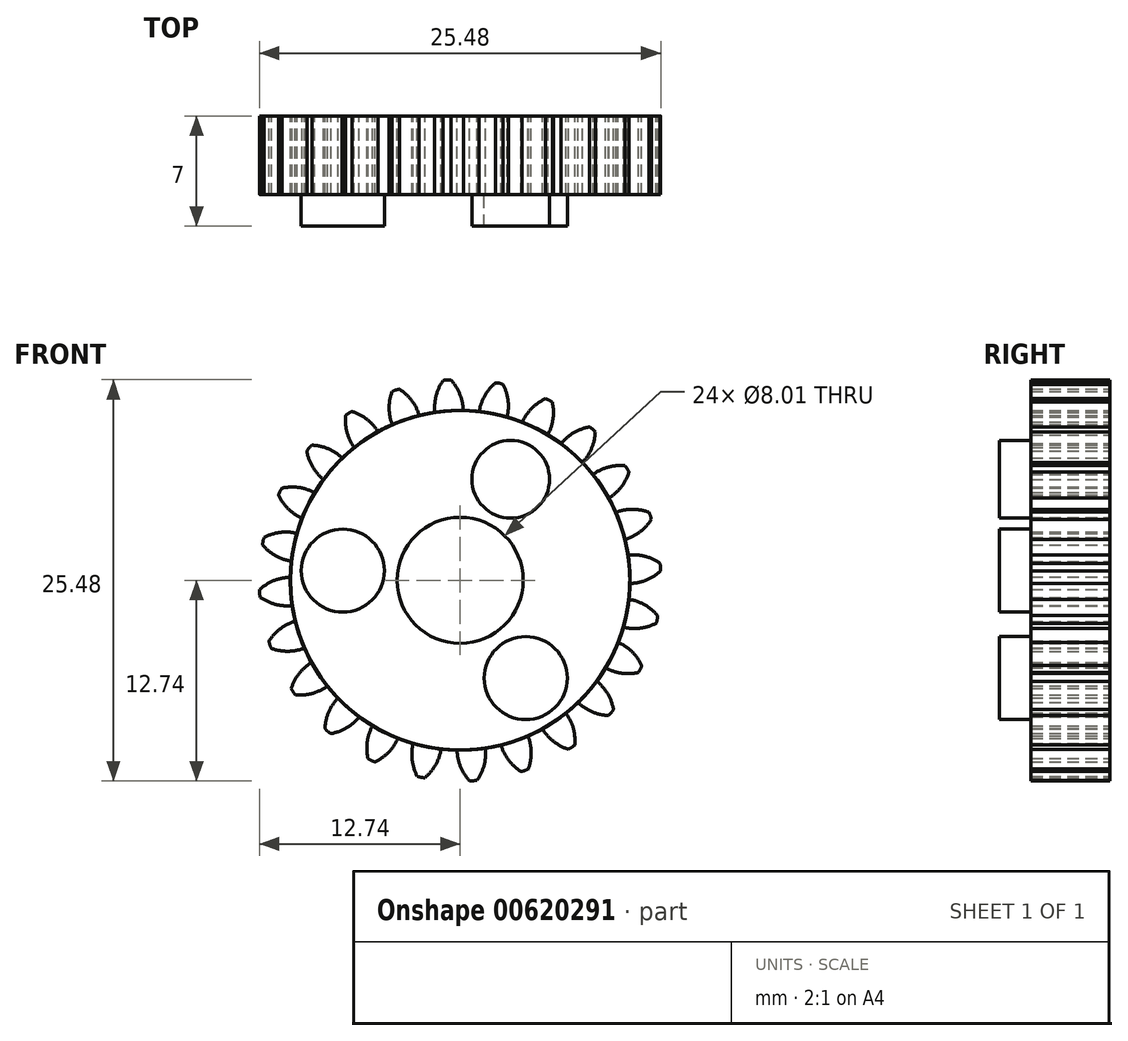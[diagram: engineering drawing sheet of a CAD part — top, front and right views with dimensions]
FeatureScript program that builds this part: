
annotation { "Feature Type Name" : "Feature", "Feature Type Description" : "" }
export const myFeature = defineFeature(function(context is Context, id is Id, definition is map)
    precondition{}
    {
        {
            var Q0;
            Q0=qCreatedBy(makeId("Front.planeOp"),FACE);
            var sketch = newSketch(context, id + "F0", { "sketchPlane" : qUnion([Q0])});
            skCircle(sketch, "E0", {"center": v(0, 0) * mm, "radius": 6.34 * mm});
            skCircle(sketch, "E1", {"center": v(0, 0) * mm, "radius": 6.93 * mm, "construction": true});
            skCircle(sketch, "E2", {"center": v(0, 0) * mm, "radius": 7.5 * mm, "construction": true});
            skLineSegment(sketch, "E3", {"start": v(0, 0) * mm, "end": v(0, 11.09) * mm, "construction": true});
            skLineSegment(sketch, "E4", {"start": v(0, 0) * mm, "end": v(-0.73, 11.09) * mm, "construction": true});
            skLineSegment(sketch, "E5", {"start": v(0, 6.93) * mm, "end": v(-9.56, 6.93) * mm, "construction": true});
            skLineSegment(sketch, "E6", {"start": v(0, 6.93) * mm, "end": v(-10.36, 3.16) * mm, "construction": true});
            skCircle(sketch, "E7", {"center": v(0, 6.93) * mm, "radius": 1.73 * mm, "construction": true});
            skCircle(sketch, "E8", {"center": v(0, 0) * mm, "radius": 6.51 * mm, "construction": true});
            skCircle(sketch, "E9", {"center": v(-1.6, 6.31) * mm, "radius": 1.73 * mm, "construction": true});
            skArc(sketch, "E10", {"start": v(0, 6.93) * mm, "mid": v(-0.15, 7.22) * mm, "end": v(-0.35, 7.49) * mm});
            skArc(sketch, "E11", {"start": v(0.12, 6.34) * mm, "mid": v(0.08, 6.64) * mm, "end": v(0, 6.93) * mm});
            skArc(sketch, "E12.MirrorCS", {"start": v(-0.9, 6.87) * mm, "mid": v(-0.8, 7.18) * mm, "end": v(-0.63, 7.47) * mm});
            skArc(sketch, "E13.MirrorCS", {"start": v(-0.94, 6.27) * mm, "mid": v(-0.95, 6.57) * mm, "end": v(-0.9, 6.87) * mm});
            skArc(sketch, "E14", {"start": v(-0.35, 7.49) * mm, "mid": v(-0.5, 7.5) * mm, "end": v(-0.63, 7.47) * mm});
            skCircle(sketch, "E15", {"center": v(0, 0) * mm, "radius": 2.35 * mm});
            skSolve(sketch);
        }
        {
            var Q0;
            {var subQ0=sQuery(id+"F0.wireOp",EDGE,"E0");var subQ1=makeQuery(id+"F0.imprint","INTERSECT",VERTEX,{"derivedFrom":[subQ0,sQuery(id+"F0.wireOp",EDGE,"E11")]});Q0=makeQuery(id+"F0.imprint","IMPRINT",FACE,{"disambiguationData":[TD([[makeQuery(id+"F0.imprint","IMPRINT",EDGE,{"disambiguationData":[TD([[subQ1,-1.0]])],"derivedFrom":subQ0}),1.0]])]});}
            var Q1;
            Q1=makeQuery(id+"F0.imprint","IMPRINT",FACE,{"disambiguationData":[TD([[makeQuery(id+"F0.imprint","IMPRINT",EDGE,{"derivedFrom":sQuery(id+"F0.wireOp",EDGE,"E10")}),1.0]])]});
            extrude(context, id + "F1", {"entities" : qUnion([Q0, Q1]), "depth" : 2.94 * mm, "offsetDistance" : 25 * mm});
        }
        {
            var Q0;
            Q0=makeQuery(id+"F1.opExtrude","SWEPT_BODY",BODY,{"disambiguationData":[OSD([sQuery(id+"F0.wireOp",EDGE,"E0"),sQuery(id+"F0.wireOp",EDGE,"E10"),sQuery(id+"F0.wireOp",EDGE,"E11"),sQuery(id+"F0.wireOp",EDGE,"E12.MirrorCS"),sQuery(id+"F0.wireOp",EDGE,"E13.MirrorCS"),sQuery(id+"F0.wireOp",EDGE,"E14")])]});
            var Q1;
            Q1=makeQuery(id+"F1.opExtrude","SWEPT_FACE",FACE,{"disambiguationData":[OSD([sQuery(id+"F0.wireOp",EDGE,"E0")])]});
            circularPattern(context, id + "F2", {"entities" : qUnion([Q0]), "axis" : qUnion([Q1]), "angle" : 360 * degree, "instanceCount" : 24, "equalSpace" : true});
        }
        {
            var Q0;
            Q0=makeQuery(id+"F2.opPattern","COPY",BODY,{"derivedFrom":makeQuery(id+"F1.opExtrude","SWEPT_BODY",BODY,{"disambiguationData":[OSD([sQuery(id+"F0.wireOp",EDGE,"E0"),sQuery(id+"F0.wireOp",EDGE,"E10"),sQuery(id+"F0.wireOp",EDGE,"E11"),sQuery(id+"F0.wireOp",EDGE,"E12.MirrorCS"),sQuery(id+"F0.wireOp",EDGE,"E13.MirrorCS"),sQuery(id+"F0.wireOp",EDGE,"E14")])]}),"instanceName":"23"});
            var Q1;
            Q1=makeQuery(id+"F2.opPattern","COPY",BODY,{"derivedFrom":makeQuery(id+"F1.opExtrude","SWEPT_BODY",BODY,{"disambiguationData":[OSD([sQuery(id+"F0.wireOp",EDGE,"E0"),sQuery(id+"F0.wireOp",EDGE,"E10"),sQuery(id+"F0.wireOp",EDGE,"E11"),sQuery(id+"F0.wireOp",EDGE,"E12.MirrorCS"),sQuery(id+"F0.wireOp",EDGE,"E13.MirrorCS"),sQuery(id+"F0.wireOp",EDGE,"E14")])]}),"instanceName":"11"});
            var Q2;
            Q2=makeQuery(id+"F2.opPattern","COPY",BODY,{"derivedFrom":makeQuery(id+"F1.opExtrude","SWEPT_BODY",BODY,{"disambiguationData":[OSD([sQuery(id+"F0.wireOp",EDGE,"E0"),sQuery(id+"F0.wireOp",EDGE,"E10"),sQuery(id+"F0.wireOp",EDGE,"E11"),sQuery(id+"F0.wireOp",EDGE,"E12.MirrorCS"),sQuery(id+"F0.wireOp",EDGE,"E13.MirrorCS"),sQuery(id+"F0.wireOp",EDGE,"E14")])]}),"instanceName":"12"});
            var Q3;
            Q3=makeQuery(id+"F2.opPattern","COPY",BODY,{"derivedFrom":makeQuery(id+"F1.opExtrude","SWEPT_BODY",BODY,{"disambiguationData":[OSD([sQuery(id+"F0.wireOp",EDGE,"E0"),sQuery(id+"F0.wireOp",EDGE,"E10"),sQuery(id+"F0.wireOp",EDGE,"E11"),sQuery(id+"F0.wireOp",EDGE,"E12.MirrorCS"),sQuery(id+"F0.wireOp",EDGE,"E13.MirrorCS"),sQuery(id+"F0.wireOp",EDGE,"E14")])]}),"instanceName":"3"});
            var Q4;
            Q4=makeQuery(id+"F2.opPattern","COPY",BODY,{"derivedFrom":makeQuery(id+"F1.opExtrude","SWEPT_BODY",BODY,{"disambiguationData":[OSD([sQuery(id+"F0.wireOp",EDGE,"E0"),sQuery(id+"F0.wireOp",EDGE,"E10"),sQuery(id+"F0.wireOp",EDGE,"E11"),sQuery(id+"F0.wireOp",EDGE,"E12.MirrorCS"),sQuery(id+"F0.wireOp",EDGE,"E13.MirrorCS"),sQuery(id+"F0.wireOp",EDGE,"E14")])]}),"instanceName":"13"});
            var Q5;
            Q5=makeQuery(id+"F2.opPattern","COPY",BODY,{"derivedFrom":makeQuery(id+"F1.opExtrude","SWEPT_BODY",BODY,{"disambiguationData":[OSD([sQuery(id+"F0.wireOp",EDGE,"E0"),sQuery(id+"F0.wireOp",EDGE,"E10"),sQuery(id+"F0.wireOp",EDGE,"E11"),sQuery(id+"F0.wireOp",EDGE,"E12.MirrorCS"),sQuery(id+"F0.wireOp",EDGE,"E13.MirrorCS"),sQuery(id+"F0.wireOp",EDGE,"E14")])]}),"instanceName":"7"});
            var Q6;
            Q6=makeQuery(id+"F2.opPattern","COPY",BODY,{"derivedFrom":makeQuery(id+"F1.opExtrude","SWEPT_BODY",BODY,{"disambiguationData":[OSD([sQuery(id+"F0.wireOp",EDGE,"E0"),sQuery(id+"F0.wireOp",EDGE,"E10"),sQuery(id+"F0.wireOp",EDGE,"E11"),sQuery(id+"F0.wireOp",EDGE,"E12.MirrorCS"),sQuery(id+"F0.wireOp",EDGE,"E13.MirrorCS"),sQuery(id+"F0.wireOp",EDGE,"E14")])]}),"instanceName":"8"});
            var Q7;
            Q7=makeQuery(id+"F2.opPattern","COPY",BODY,{"derivedFrom":makeQuery(id+"F1.opExtrude","SWEPT_BODY",BODY,{"disambiguationData":[OSD([sQuery(id+"F0.wireOp",EDGE,"E0"),sQuery(id+"F0.wireOp",EDGE,"E10"),sQuery(id+"F0.wireOp",EDGE,"E11"),sQuery(id+"F0.wireOp",EDGE,"E12.MirrorCS"),sQuery(id+"F0.wireOp",EDGE,"E13.MirrorCS"),sQuery(id+"F0.wireOp",EDGE,"E14")])]}),"instanceName":"1"});
            var Q8;
            Q8=makeQuery(id+"F2.opPattern","COPY",BODY,{"derivedFrom":makeQuery(id+"F1.opExtrude","SWEPT_BODY",BODY,{"disambiguationData":[OSD([sQuery(id+"F0.wireOp",EDGE,"E0"),sQuery(id+"F0.wireOp",EDGE,"E10"),sQuery(id+"F0.wireOp",EDGE,"E11"),sQuery(id+"F0.wireOp",EDGE,"E12.MirrorCS"),sQuery(id+"F0.wireOp",EDGE,"E13.MirrorCS"),sQuery(id+"F0.wireOp",EDGE,"E14")])]}),"instanceName":"14"});
            var Q9;
            Q9=makeQuery(id+"F2.opPattern","COPY",BODY,{"derivedFrom":makeQuery(id+"F1.opExtrude","SWEPT_BODY",BODY,{"disambiguationData":[OSD([sQuery(id+"F0.wireOp",EDGE,"E0"),sQuery(id+"F0.wireOp",EDGE,"E10"),sQuery(id+"F0.wireOp",EDGE,"E11"),sQuery(id+"F0.wireOp",EDGE,"E12.MirrorCS"),sQuery(id+"F0.wireOp",EDGE,"E13.MirrorCS"),sQuery(id+"F0.wireOp",EDGE,"E14")])]}),"instanceName":"21"});
            var Q10;
            Q10=makeQuery(id+"F2.opPattern","COPY",BODY,{"derivedFrom":makeQuery(id+"F1.opExtrude","SWEPT_BODY",BODY,{"disambiguationData":[OSD([sQuery(id+"F0.wireOp",EDGE,"E0"),sQuery(id+"F0.wireOp",EDGE,"E10"),sQuery(id+"F0.wireOp",EDGE,"E11"),sQuery(id+"F0.wireOp",EDGE,"E12.MirrorCS"),sQuery(id+"F0.wireOp",EDGE,"E13.MirrorCS"),sQuery(id+"F0.wireOp",EDGE,"E14")])]}),"instanceName":"9"});
            var Q11;
            Q11=makeQuery(id+"F2.opPattern","COPY",BODY,{"derivedFrom":makeQuery(id+"F1.opExtrude","SWEPT_BODY",BODY,{"disambiguationData":[OSD([sQuery(id+"F0.wireOp",EDGE,"E0"),sQuery(id+"F0.wireOp",EDGE,"E10"),sQuery(id+"F0.wireOp",EDGE,"E11"),sQuery(id+"F0.wireOp",EDGE,"E12.MirrorCS"),sQuery(id+"F0.wireOp",EDGE,"E13.MirrorCS"),sQuery(id+"F0.wireOp",EDGE,"E14")])]}),"instanceName":"2"});
            var Q12;
            Q12=makeQuery(id+"F1.opExtrude","SWEPT_BODY",BODY,{"disambiguationData":[OSD([sQuery(id+"F0.wireOp",EDGE,"E0"),sQuery(id+"F0.wireOp",EDGE,"E10"),sQuery(id+"F0.wireOp",EDGE,"E11"),sQuery(id+"F0.wireOp",EDGE,"E12.MirrorCS"),sQuery(id+"F0.wireOp",EDGE,"E13.MirrorCS"),sQuery(id+"F0.wireOp",EDGE,"E14")])]});
            var Q13;
            Q13=makeQuery(id+"F2.opPattern","COPY",BODY,{"derivedFrom":makeQuery(id+"F1.opExtrude","SWEPT_BODY",BODY,{"disambiguationData":[OSD([sQuery(id+"F0.wireOp",EDGE,"E0"),sQuery(id+"F0.wireOp",EDGE,"E10"),sQuery(id+"F0.wireOp",EDGE,"E11"),sQuery(id+"F0.wireOp",EDGE,"E12.MirrorCS"),sQuery(id+"F0.wireOp",EDGE,"E13.MirrorCS"),sQuery(id+"F0.wireOp",EDGE,"E14")])]}),"instanceName":"22"});
            var Q14;
            Q14=makeQuery(id+"F2.opPattern","COPY",BODY,{"derivedFrom":makeQuery(id+"F1.opExtrude","SWEPT_BODY",BODY,{"disambiguationData":[OSD([sQuery(id+"F0.wireOp",EDGE,"E0"),sQuery(id+"F0.wireOp",EDGE,"E10"),sQuery(id+"F0.wireOp",EDGE,"E11"),sQuery(id+"F0.wireOp",EDGE,"E12.MirrorCS"),sQuery(id+"F0.wireOp",EDGE,"E13.MirrorCS"),sQuery(id+"F0.wireOp",EDGE,"E14")])]}),"instanceName":"4"});
            var Q15;
            Q15=makeQuery(id+"F2.opPattern","COPY",BODY,{"derivedFrom":makeQuery(id+"F1.opExtrude","SWEPT_BODY",BODY,{"disambiguationData":[OSD([sQuery(id+"F0.wireOp",EDGE,"E0"),sQuery(id+"F0.wireOp",EDGE,"E10"),sQuery(id+"F0.wireOp",EDGE,"E11"),sQuery(id+"F0.wireOp",EDGE,"E12.MirrorCS"),sQuery(id+"F0.wireOp",EDGE,"E13.MirrorCS"),sQuery(id+"F0.wireOp",EDGE,"E14")])]}),"instanceName":"16"});
            var Q16;
            Q16=makeQuery(id+"F2.opPattern","COPY",BODY,{"derivedFrom":makeQuery(id+"F1.opExtrude","SWEPT_BODY",BODY,{"disambiguationData":[OSD([sQuery(id+"F0.wireOp",EDGE,"E0"),sQuery(id+"F0.wireOp",EDGE,"E10"),sQuery(id+"F0.wireOp",EDGE,"E11"),sQuery(id+"F0.wireOp",EDGE,"E12.MirrorCS"),sQuery(id+"F0.wireOp",EDGE,"E13.MirrorCS"),sQuery(id+"F0.wireOp",EDGE,"E14")])]}),"instanceName":"10"});
            var Q17;
            Q17=makeQuery(id+"F2.opPattern","COPY",BODY,{"derivedFrom":makeQuery(id+"F1.opExtrude","SWEPT_BODY",BODY,{"disambiguationData":[OSD([sQuery(id+"F0.wireOp",EDGE,"E0"),sQuery(id+"F0.wireOp",EDGE,"E10"),sQuery(id+"F0.wireOp",EDGE,"E11"),sQuery(id+"F0.wireOp",EDGE,"E12.MirrorCS"),sQuery(id+"F0.wireOp",EDGE,"E13.MirrorCS"),sQuery(id+"F0.wireOp",EDGE,"E14")])]}),"instanceName":"17"});
            var Q18;
            Q18=makeQuery(id+"F2.opPattern","COPY",BODY,{"derivedFrom":makeQuery(id+"F1.opExtrude","SWEPT_BODY",BODY,{"disambiguationData":[OSD([sQuery(id+"F0.wireOp",EDGE,"E0"),sQuery(id+"F0.wireOp",EDGE,"E10"),sQuery(id+"F0.wireOp",EDGE,"E11"),sQuery(id+"F0.wireOp",EDGE,"E12.MirrorCS"),sQuery(id+"F0.wireOp",EDGE,"E13.MirrorCS"),sQuery(id+"F0.wireOp",EDGE,"E14")])]}),"instanceName":"15"});
            var Q19;
            Q19=makeQuery(id+"F2.opPattern","COPY",BODY,{"derivedFrom":makeQuery(id+"F1.opExtrude","SWEPT_BODY",BODY,{"disambiguationData":[OSD([sQuery(id+"F0.wireOp",EDGE,"E0"),sQuery(id+"F0.wireOp",EDGE,"E10"),sQuery(id+"F0.wireOp",EDGE,"E11"),sQuery(id+"F0.wireOp",EDGE,"E12.MirrorCS"),sQuery(id+"F0.wireOp",EDGE,"E13.MirrorCS"),sQuery(id+"F0.wireOp",EDGE,"E14")])]}),"instanceName":"5"});
            var Q20;
            Q20=makeQuery(id+"F2.opPattern","COPY",BODY,{"derivedFrom":makeQuery(id+"F1.opExtrude","SWEPT_BODY",BODY,{"disambiguationData":[OSD([sQuery(id+"F0.wireOp",EDGE,"E0"),sQuery(id+"F0.wireOp",EDGE,"E10"),sQuery(id+"F0.wireOp",EDGE,"E11"),sQuery(id+"F0.wireOp",EDGE,"E12.MirrorCS"),sQuery(id+"F0.wireOp",EDGE,"E13.MirrorCS"),sQuery(id+"F0.wireOp",EDGE,"E14")])]}),"instanceName":"6"});
            var Q21;
            Q21=makeQuery(id+"F2.opPattern","COPY",BODY,{"derivedFrom":makeQuery(id+"F1.opExtrude","SWEPT_BODY",BODY,{"disambiguationData":[OSD([sQuery(id+"F0.wireOp",EDGE,"E0"),sQuery(id+"F0.wireOp",EDGE,"E10"),sQuery(id+"F0.wireOp",EDGE,"E11"),sQuery(id+"F0.wireOp",EDGE,"E12.MirrorCS"),sQuery(id+"F0.wireOp",EDGE,"E13.MirrorCS"),sQuery(id+"F0.wireOp",EDGE,"E14")])]}),"instanceName":"20"});
            var Q22;
            Q22=makeQuery(id+"F2.opPattern","COPY",BODY,{"derivedFrom":makeQuery(id+"F1.opExtrude","SWEPT_BODY",BODY,{"disambiguationData":[OSD([sQuery(id+"F0.wireOp",EDGE,"E0"),sQuery(id+"F0.wireOp",EDGE,"E10"),sQuery(id+"F0.wireOp",EDGE,"E11"),sQuery(id+"F0.wireOp",EDGE,"E12.MirrorCS"),sQuery(id+"F0.wireOp",EDGE,"E13.MirrorCS"),sQuery(id+"F0.wireOp",EDGE,"E14")])]}),"instanceName":"19"});
            var Q23;
            Q23=makeQuery(id+"F2.opPattern","COPY",BODY,{"derivedFrom":makeQuery(id+"F1.opExtrude","SWEPT_BODY",BODY,{"disambiguationData":[OSD([sQuery(id+"F0.wireOp",EDGE,"E0"),sQuery(id+"F0.wireOp",EDGE,"E10"),sQuery(id+"F0.wireOp",EDGE,"E11"),sQuery(id+"F0.wireOp",EDGE,"E12.MirrorCS"),sQuery(id+"F0.wireOp",EDGE,"E13.MirrorCS"),sQuery(id+"F0.wireOp",EDGE,"E14")])]}),"instanceName":"18"});
            var Q24;
            Q24=sQuery(id+"F0.wireOp",VERTEX,"E0.center");
            transform(context, id + "F3", {"entities" : qUnion([Q0, Q1, Q2, Q3, Q4, Q5, Q6, Q7, Q8, Q9, Q10, Q11, Q12, Q13, Q14, Q15, Q16, Q17, Q18, Q19, Q20, Q21, Q22, Q23]), "transformType" : TransformType.SCALE_UNIFORMLY, "scale" : 1.7, "scalePoint" : qUnion([Q24]), "makeCopy" : false});
        }
        {
            var Q0;
            Q0=makeQuery(id+"F0.imprint","IMPRINT",FACE,{"disambiguationData":[TD([[makeQuery(id+"F0.imprint","IMPRINT",EDGE,{"derivedFrom":sQuery(id+"F0.wireOp",EDGE,"E15")}),1.0]])]});
            extrude(context, id + "F4", {"entities" : qUnion([Q0]), "operationType" : NewBodyOperationType.REMOVE, "endBound" : BoundingType.SYMMETRIC, "depth" : 220 * mm, "offsetDistance" : 25 * mm});
        }
        {
            var Q0;
            Q0=makeQuery(id+"F2.opPattern","COPY",FACE,{"derivedFrom":makeQuery(id+"F1.opExtrude","CAP_FACE",FACE,{"disambiguationData":[OSD([sQuery(id+"F0.wireOp",EDGE,"E0"),sQuery(id+"F0.wireOp",EDGE,"E10"),sQuery(id+"F0.wireOp",EDGE,"E11"),sQuery(id+"F0.wireOp",EDGE,"E12.MirrorCS"),sQuery(id+"F0.wireOp",EDGE,"E13.MirrorCS"),sQuery(id+"F0.wireOp",EDGE,"E14"),sQuery(id+"F0.wireOp",EDGE,"E15")])],"isStart":false}),"instanceName":"13"});
            var sketch = newSketch(context, id + "F5", { "sketchPlane" : qUnion([Q0])});
            skCircle(sketch, "E16", {"center": v(0, 0) * mm, "radius": 4 * mm});
            skSolve(sketch);
        }
        {
            var Q0;
            Q0 = qSketchRegion(id + "F5", true);
            extrude(context, id + "F6", {"entities" : qUnion([Q0]), "operationType" : NewBodyOperationType.REMOVE, "endBound" : BoundingType.SYMMETRIC, "oppositeDirection" : true, "depth" : 25 * mm, "offsetDistance" : 25 * mm});
        }
        {
            var Q0;
            Q0=makeQuery(id+"F1.opExtrude","CAP_FACE",FACE,{"disambiguationData":[OSD([sQuery(id+"F0.wireOp",EDGE,"E0"),sQuery(id+"F0.wireOp",EDGE,"E10"),sQuery(id+"F0.wireOp",EDGE,"E11"),sQuery(id+"F0.wireOp",EDGE,"E12.MirrorCS"),sQuery(id+"F0.wireOp",EDGE,"E13.MirrorCS"),sQuery(id+"F0.wireOp",EDGE,"E14"),sQuery(id+"F0.wireOp",EDGE,"E15")])],"isStart":false});
            var sketch = newSketch(context, id + "F7", { "sketchPlane" : qUnion([Q0])});
            skCircle(sketch, "E17", {"center": v(3.21, 6.42) * mm, "radius": 2.46 * mm});
            skPoint(sketch, "E17.first.point", {"position": v(3.08, 8.88) * mm});
            skPoint(sketch, "E17.second.point", {"position": v(3.42, 3.96) * mm});
            skPoint(sketch, "E17.third.point", {"position": v(4.67, 4.43) * mm});
            skCircle(sketch, "E18", {"center": v(-7.45, 0.61) * mm, "radius": 2.64 * mm});
            skPoint(sketch, "E18.first.point", {"position": v(-8.57, 3) * mm});
            skPoint(sketch, "E18.second.point", {"position": v(-4.84, 1) * mm});
            skPoint(sketch, "E18.third.point", {"position": v(-5.41, -1.06) * mm});
            skCircle(sketch, "E19", {"center": v(4.17, -6.21) * mm, "radius": 2.64 * mm});
            skPoint(sketch, "E19.first.point", {"position": v(2.61, -4.08) * mm});
            skPoint(sketch, "E19.second.point", {"position": v(5.68, -8.37) * mm});
            skPoint(sketch, "E19.third.point", {"position": v(3.23, -8.68) * mm});
            skSolve(sketch);
        }
        {
            var Q0;
            Q0 = qSketchRegion(id + "F7", true);
            extrude(context, id + "F8", {"entities" : qUnion([Q0]), "depth" : 2 * mm, "offsetDistance" : 25 * mm});
        }
    });
